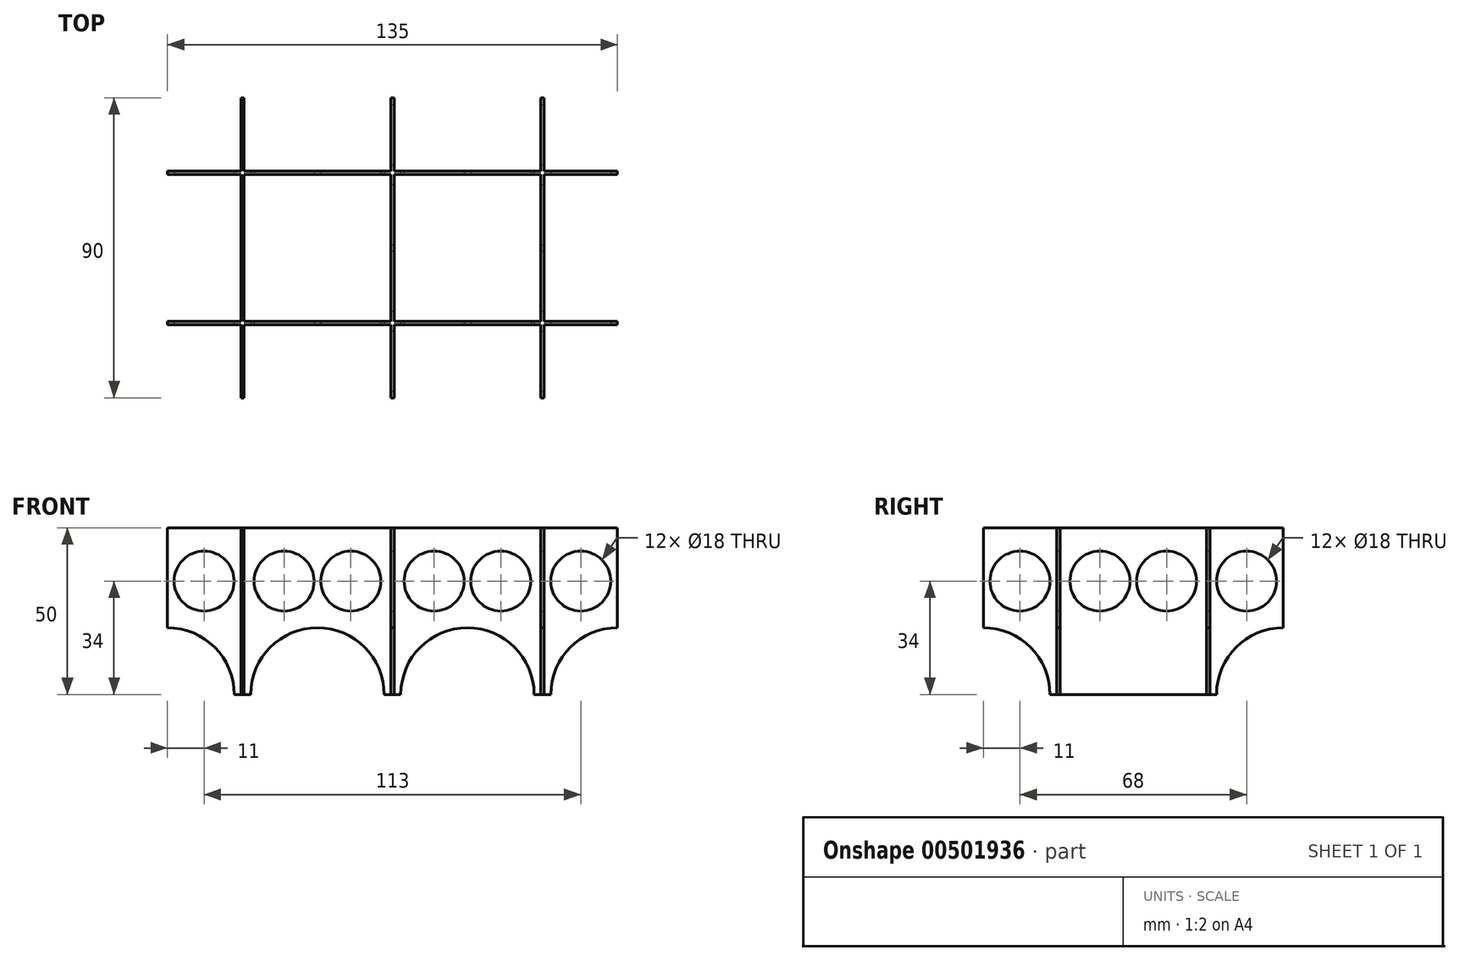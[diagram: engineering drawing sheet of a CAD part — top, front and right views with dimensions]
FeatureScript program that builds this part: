
annotation { "Feature Type Name" : "Feature", "Feature Type Description" : "" }
export const myFeature = defineFeature(function(context is Context, id is Id, definition is map)
    precondition{}
    {
        {
            var Q0;
            Q0=qCreatedBy(makeId("Top.planeOp"),FACE);
            var sketch = newSketch(context, id + "F0", { "sketchPlane" : qUnion([Q0])});
            skPoint(sketch, "E0", {"position": v(0, -22.5) * mm});
            skPoint(sketch, "E1", {"position": v(0, 22.5) * mm});
            skPoint(sketch, "E2", {"position": v(-45, 0) * mm});
            skPoint(sketch, "E3", {"position": v(45, 0) * mm});
            skLineSegment(sketch, "E4.bottom", {"start": v(67.5, 22) * mm, "end": v(-67.5, 22) * mm});
            skLineSegment(sketch, "E4.top", {"start": v(67.5, 23) * mm, "end": v(-67.5, 23) * mm});
            skLineSegment(sketch, "E4.left", {"start": v(67.5, 22) * mm, "end": v(67.5, 23) * mm});
            skLineSegment(sketch, "E4.right", {"start": v(-67.5, 22) * mm, "end": v(-67.5, 23) * mm});
            skLineSegment(sketch, "E5.bottom", {"start": v(67.5, -23) * mm, "end": v(-67.5, -23) * mm});
            skLineSegment(sketch, "E5.top", {"start": v(67.5, -22) * mm, "end": v(-67.5, -22) * mm});
            skLineSegment(sketch, "E5.left", {"start": v(67.5, -23) * mm, "end": v(67.5, -22) * mm});
            skLineSegment(sketch, "E5.right", {"start": v(-67.5, -23) * mm, "end": v(-67.5, -22) * mm});
            skLineSegment(sketch, "E6.bottom", {"start": v(-44.5, -45) * mm, "end": v(-45.5, -45) * mm});
            skLineSegment(sketch, "E6.top", {"start": v(-44.5, 45) * mm, "end": v(-45.5, 45) * mm});
            skLineSegment(sketch, "E6.left", {"start": v(-44.5, -45) * mm, "end": v(-44.5, 45) * mm});
            skLineSegment(sketch, "E6.right", {"start": v(-45.5, -45) * mm, "end": v(-45.5, 45) * mm});
            skLineSegment(sketch, "E7.bottom", {"start": v(45.5, -45) * mm, "end": v(44.5, -45) * mm});
            skLineSegment(sketch, "E7.top", {"start": v(45.5, 45) * mm, "end": v(44.5, 45) * mm});
            skLineSegment(sketch, "E7.left", {"start": v(45.5, -45) * mm, "end": v(45.5, 45) * mm});
            skLineSegment(sketch, "E7.right", {"start": v(44.5, -45) * mm, "end": v(44.5, 45) * mm});
            skLineSegment(sketch, "E8.bottom", {"start": v(0.5, -45) * mm, "end": v(-0.5, -45) * mm});
            skLineSegment(sketch, "E8.top", {"start": v(0.5, 45) * mm, "end": v(-0.5, 45) * mm});
            skLineSegment(sketch, "E8.left", {"start": v(0.5, -45) * mm, "end": v(0.5, 45) * mm});
            skLineSegment(sketch, "E8.right", {"start": v(-0.5, -45) * mm, "end": v(-0.5, 45) * mm});
            skPoint(sketch, "E8.middle", {"position": v(0, 0) * mm});
            skSolve(sketch);
        }
        {
            var Q0;
            {var subQ5=sQuery(id+"F0.wireOp",EDGE,"E6.top");Q0=makeQuery(id+"F0.imprint","IMPRINT",FACE,{"disambiguationData":[TD([[makeQuery(id+"F0.imprint","IMPRINT",EDGE,{"derivedFrom":subQ5}),1.0]])]});}
            var Q1;
            {var subQ0=sQuery(id+"F0.wireOp",EDGE,"E4.right");Q1=makeQuery(id+"F0.imprint","IMPRINT",FACE,{"disambiguationData":[TD([[makeQuery(id+"F0.imprint","IMPRINT",EDGE,{"derivedFrom":subQ0}),-1.0]])]});}
            var Q2;
            {var subQ0=sQuery(id+"F0.wireOp",EDGE,"E8.right");var subQ1=sQuery(id+"F0.wireOp",EDGE,"E4.bottom");var subQ2=makeQuery(id+"F0.imprint","INTERSECT",VERTEX,{"derivedFrom":[subQ1,subQ0]});Q2=makeQuery(id+"F0.imprint","IMPRINT",FACE,{"disambiguationData":[TD([[makeQuery(id+"F0.imprint","IMPRINT",EDGE,{"disambiguationData":[TD([[subQ2,-1.0]])],"derivedFrom":subQ1}),-1.0]])]});}
            var Q3;
            {var subQ0=sQuery(id+"F0.wireOp",EDGE,"E6.right");var subQ1=sQuery(id+"F0.wireOp",EDGE,"E4.bottom");var subQ2=makeQuery(id+"F0.imprint","INTERSECT",VERTEX,{"derivedFrom":[subQ1,subQ0]});Q3=makeQuery(id+"F0.imprint","IMPRINT",FACE,{"disambiguationData":[TD([[makeQuery(id+"F0.imprint","IMPRINT",EDGE,{"disambiguationData":[TD([[subQ2,1.0]])],"derivedFrom":subQ1}),1.0]])]});}
            var Q4;
            {var subQ0=sQuery(id+"F0.wireOp",EDGE,"E6.right");var subQ1=sQuery(id+"F0.wireOp",EDGE,"E4.bottom");var subQ2=makeQuery(id+"F0.imprint","INTERSECT",VERTEX,{"derivedFrom":[subQ1,subQ0]});Q4=makeQuery(id+"F0.imprint","IMPRINT",FACE,{"disambiguationData":[TD([[makeQuery(id+"F0.imprint","IMPRINT",EDGE,{"disambiguationData":[TD([[subQ2,1.0]])],"derivedFrom":subQ1}),-1.0]])]});}
            var Q5;
            {var subQ0=sQuery(id+"F0.wireOp",EDGE,"E8.left");var subQ1=sQuery(id+"F0.wireOp",EDGE,"E4.bottom");var subQ2=makeQuery(id+"F0.imprint","INTERSECT",VERTEX,{"derivedFrom":[subQ1,subQ0]});Q5=makeQuery(id+"F0.imprint","IMPRINT",FACE,{"disambiguationData":[TD([[makeQuery(id+"F0.imprint","IMPRINT",EDGE,{"disambiguationData":[TD([[subQ2,-1.0]])],"derivedFrom":subQ1}),-1.0]])]});}
            var Q6;
            {var subQ5=sQuery(id+"F0.wireOp",EDGE,"E8.top");Q6=makeQuery(id+"F0.imprint","IMPRINT",FACE,{"disambiguationData":[TD([[makeQuery(id+"F0.imprint","IMPRINT",EDGE,{"derivedFrom":subQ5}),1.0]])]});}
            var Q7;
            {var subQ0=sQuery(id+"F0.wireOp",EDGE,"E7.right");var subQ1=sQuery(id+"F0.wireOp",EDGE,"E4.bottom");var subQ2=makeQuery(id+"F0.imprint","INTERSECT",VERTEX,{"derivedFrom":[subQ1,subQ0]});Q7=makeQuery(id+"F0.imprint","IMPRINT",FACE,{"disambiguationData":[TD([[makeQuery(id+"F0.imprint","IMPRINT",EDGE,{"disambiguationData":[TD([[subQ2,-1.0]])],"derivedFrom":subQ1}),-1.0]])]});}
            var Q8;
            {var subQ0=sQuery(id+"F0.wireOp",EDGE,"E8.left");var subQ1=sQuery(id+"F0.wireOp",EDGE,"E4.bottom");var subQ2=makeQuery(id+"F0.imprint","INTERSECT",VERTEX,{"derivedFrom":[subQ1,subQ0]});Q8=makeQuery(id+"F0.imprint","IMPRINT",FACE,{"disambiguationData":[TD([[makeQuery(id+"F0.imprint","IMPRINT",EDGE,{"disambiguationData":[TD([[subQ2,-1.0]])],"derivedFrom":subQ1}),1.0]])]});}
            var Q9;
            {var subQ0=sQuery(id+"F0.wireOp",EDGE,"E7.left");var subQ1=sQuery(id+"F0.wireOp",EDGE,"E4.bottom");var subQ2=makeQuery(id+"F0.imprint","INTERSECT",VERTEX,{"derivedFrom":[subQ1,subQ0]});Q9=makeQuery(id+"F0.imprint","IMPRINT",FACE,{"disambiguationData":[TD([[makeQuery(id+"F0.imprint","IMPRINT",EDGE,{"disambiguationData":[TD([[subQ2,-1.0]])],"derivedFrom":subQ1}),-1.0]])]});}
            var Q10;
            {var subQ0=sQuery(id+"F0.wireOp",EDGE,"E4.left");Q10=makeQuery(id+"F0.imprint","IMPRINT",FACE,{"disambiguationData":[TD([[makeQuery(id+"F0.imprint","IMPRINT",EDGE,{"derivedFrom":subQ0}),1.0]])]});}
            var Q11;
            {var subQ5=sQuery(id+"F0.wireOp",EDGE,"E7.top");Q11=makeQuery(id+"F0.imprint","IMPRINT",FACE,{"disambiguationData":[TD([[makeQuery(id+"F0.imprint","IMPRINT",EDGE,{"derivedFrom":subQ5}),1.0]])]});}
            var Q12;
            {var subQ0=sQuery(id+"F0.wireOp",EDGE,"E7.left");var subQ1=sQuery(id+"F0.wireOp",EDGE,"E4.bottom");var subQ2=makeQuery(id+"F0.imprint","INTERSECT",VERTEX,{"derivedFrom":[subQ1,subQ0]});Q12=makeQuery(id+"F0.imprint","IMPRINT",FACE,{"disambiguationData":[TD([[makeQuery(id+"F0.imprint","IMPRINT",EDGE,{"disambiguationData":[TD([[subQ2,-1.0]])],"derivedFrom":subQ1}),1.0]])]});}
            var Q13;
            {var subQ0=sQuery(id+"F0.wireOp",EDGE,"E5.left");Q13=makeQuery(id+"F0.imprint","IMPRINT",FACE,{"disambiguationData":[TD([[makeQuery(id+"F0.imprint","IMPRINT",EDGE,{"derivedFrom":subQ0}),1.0]])]});}
            var Q14;
            {var subQ5=sQuery(id+"F0.wireOp",EDGE,"E7.bottom");Q14=makeQuery(id+"F0.imprint","IMPRINT",FACE,{"disambiguationData":[TD([[makeQuery(id+"F0.imprint","IMPRINT",EDGE,{"derivedFrom":subQ5}),-1.0]])]});}
            var Q15;
            {var subQ0=sQuery(id+"F0.wireOp",EDGE,"E7.left");var subQ1=sQuery(id+"F0.wireOp",EDGE,"E5.bottom");var subQ2=makeQuery(id+"F0.imprint","INTERSECT",VERTEX,{"derivedFrom":[subQ1,subQ0]});Q15=makeQuery(id+"F0.imprint","IMPRINT",FACE,{"disambiguationData":[TD([[makeQuery(id+"F0.imprint","IMPRINT",EDGE,{"disambiguationData":[TD([[subQ2,-1.0]])],"derivedFrom":subQ1}),-1.0]])]});}
            var Q16;
            {var subQ0=sQuery(id+"F0.wireOp",EDGE,"E7.right");var subQ1=sQuery(id+"F0.wireOp",EDGE,"E5.bottom");var subQ2=makeQuery(id+"F0.imprint","INTERSECT",VERTEX,{"derivedFrom":[subQ1,subQ0]});Q16=makeQuery(id+"F0.imprint","IMPRINT",FACE,{"disambiguationData":[TD([[makeQuery(id+"F0.imprint","IMPRINT",EDGE,{"disambiguationData":[TD([[subQ2,-1.0]])],"derivedFrom":subQ1}),-1.0]])]});}
            var Q17;
            {var subQ0=sQuery(id+"F0.wireOp",EDGE,"E8.left");var subQ1=sQuery(id+"F0.wireOp",EDGE,"E5.bottom");var subQ2=makeQuery(id+"F0.imprint","INTERSECT",VERTEX,{"derivedFrom":[subQ1,subQ0]});Q17=makeQuery(id+"F0.imprint","IMPRINT",FACE,{"disambiguationData":[TD([[makeQuery(id+"F0.imprint","IMPRINT",EDGE,{"disambiguationData":[TD([[subQ2,-1.0]])],"derivedFrom":subQ1}),-1.0]])]});}
            var Q18;
            {var subQ5=sQuery(id+"F0.wireOp",EDGE,"E8.bottom");Q18=makeQuery(id+"F0.imprint","IMPRINT",FACE,{"disambiguationData":[TD([[makeQuery(id+"F0.imprint","IMPRINT",EDGE,{"derivedFrom":subQ5}),-1.0]])]});}
            var Q19;
            {var subQ0=sQuery(id+"F0.wireOp",EDGE,"E8.right");var subQ1=sQuery(id+"F0.wireOp",EDGE,"E5.bottom");var subQ2=makeQuery(id+"F0.imprint","INTERSECT",VERTEX,{"derivedFrom":[subQ1,subQ0]});Q19=makeQuery(id+"F0.imprint","IMPRINT",FACE,{"disambiguationData":[TD([[makeQuery(id+"F0.imprint","IMPRINT",EDGE,{"disambiguationData":[TD([[subQ2,-1.0]])],"derivedFrom":subQ1}),-1.0]])]});}
            var Q20;
            {var subQ0=sQuery(id+"F0.wireOp",EDGE,"E5.right");Q20=makeQuery(id+"F0.imprint","IMPRINT",FACE,{"disambiguationData":[TD([[makeQuery(id+"F0.imprint","IMPRINT",EDGE,{"derivedFrom":subQ0}),-1.0]])]});}
            var Q21;
            {var subQ5=sQuery(id+"F0.wireOp",EDGE,"E6.bottom");Q21=makeQuery(id+"F0.imprint","IMPRINT",FACE,{"disambiguationData":[TD([[makeQuery(id+"F0.imprint","IMPRINT",EDGE,{"derivedFrom":subQ5}),-1.0]])]});}
            var Q22;
            {var subQ0=sQuery(id+"F0.wireOp",EDGE,"E6.left");var subQ1=sQuery(id+"F0.wireOp",EDGE,"E5.bottom");var subQ2=makeQuery(id+"F0.imprint","INTERSECT",VERTEX,{"derivedFrom":[subQ1,subQ0]});Q22=makeQuery(id+"F0.imprint","IMPRINT",FACE,{"disambiguationData":[TD([[makeQuery(id+"F0.imprint","IMPRINT",EDGE,{"disambiguationData":[TD([[subQ2,-1.0]])],"derivedFrom":subQ1}),-1.0]])]});}
            extrude(context, id + "F1", {"entities" : qUnion([Q0, Q1, Q2, Q3, Q4, Q5, Q6, Q7, Q8, Q9, Q10, Q11, Q12, Q13, Q14, Q15, Q16, Q17, Q18, Q19, Q20, Q21, Q22]), "depth" : 50 * mm});
        }
        {
            var Q0;
            {var subQ0=sQuery(id+"F0.wireOp",EDGE,"E5.bottom");Q0=makeQuery(id+"F1.opExtrude","SWEPT_FACE",FACE,{"disambiguationData":[OSD([subQ0]),TDD([makeQuery(id+"F0.imprint","IMPRINT",EDGE,{"disambiguationData":[TD([[makeQuery(id+"F0.imprint","INTERSECT",VERTEX,{"derivedFrom":[subQ0,sQuery(id+"F0.wireOp",EDGE,"E8.right")]}),-1.0]])],"derivedFrom":subQ0})])]});}
            var sketch = newSketch(context, id + "F2", { "sketchPlane" : qUnion([Q0])});
            skPoint(sketch, "E9", {"position": v(-22.5, 0) * mm});
            skCircle(sketch, "E10", {"center": v(-22.5, 0) * mm, "radius": 20 * mm});
            skPoint(sketch, "E11", {"position": v(-32.5, 34) * mm});
            skPoint(sketch, "E12", {"position": v(-12.5, 34) * mm});
            skCircle(sketch, "E13", {"center": v(-32.5, 34) * mm, "radius": 9 * mm});
            skCircle(sketch, "E14", {"center": v(-12.5, 34) * mm, "radius": 9 * mm});
            skPoint(sketch, "E15", {"position": v(22.5, 0) * mm});
            skCircle(sketch, "E16", {"center": v(22.5, 0) * mm, "radius": 20 * mm});
            skPoint(sketch, "E17", {"position": v(12.5, 34) * mm});
            skPoint(sketch, "E18", {"position": v(32.5, 34) * mm});
            skCircle(sketch, "E19", {"center": v(12.5, 34) * mm, "radius": 9 * mm});
            skCircle(sketch, "E20", {"center": v(32.5, 34) * mm, "radius": 9 * mm});
            skCircle(sketch, "E21", {"center": v(-67.5, 0) * mm, "radius": 20 * mm});
            skPoint(sketch, "E22", {"position": v(-56.5, 34) * mm});
            skCircle(sketch, "E23", {"center": v(-56.5, 34) * mm, "radius": 9 * mm});
            skCircle(sketch, "E24", {"center": v(67.5, 0) * mm, "radius": 20 * mm});
            skPoint(sketch, "E25", {"position": v(56.5, 34) * mm});
            skCircle(sketch, "E26", {"center": v(56.5, 34) * mm, "radius": 9 * mm});
            skSolve(sketch);
        }
        {
            var Q0;
            Q0=makeQuery(id+"F2.imprint","IMPRINT",FACE,{"disambiguationData":[TD([[makeQuery(id+"F2.imprint","IMPRINT",EDGE,{"derivedFrom":sQuery(id+"F2.wireOp",EDGE,"E23")}),1.0]])]});
            var Q1;
            Q1=makeQuery(id+"F2.imprint","IMPRINT",FACE,{"disambiguationData":[TD([[makeQuery(id+"F2.imprint","IMPRINT",EDGE,{"derivedFrom":sQuery(id+"F2.wireOp",EDGE,"E21")}),1.0]])]});
            var Q2;
            {var subQ0=sQuery(id+"F2.wireOp",EDGE,"E10");var subQ1=sQuery(id+"F0.wireOp",EDGE,"E5.bottom");var subQ2=makeQuery(id+"F1.opExtrude","CAP_EDGE",EDGE,{"disambiguationData":[OSD([subQ1]),TDD([makeQuery(id+"F0.imprint","IMPRINT",EDGE,{"disambiguationData":[TD([[makeQuery(id+"F0.imprint","INTERSECT",VERTEX,{"derivedFrom":[subQ1,sQuery(id+"F0.wireOp",EDGE,"E8.right")]}),-1.0]])],"derivedFrom":subQ1})])],"isStart":true});var subQ3=makeQuery(id+"F2.imprint","INTERSECT",VERTEX,{"disambiguationData":[OD(0.0)],"derivedFrom":[subQ2,subQ0]});Q2=makeQuery(id+"F2.imprint","IMPRINT",FACE,{"disambiguationData":[TD([[makeQuery(id+"F2.imprint","IMPRINT",EDGE,{"disambiguationData":[TD([[subQ3,-1.0]])],"derivedFrom":subQ0}),1.0]])]});}
            var Q3;
            Q3=makeQuery(id+"F2.imprint","IMPRINT",FACE,{"disambiguationData":[TD([[makeQuery(id+"F2.imprint","IMPRINT",EDGE,{"derivedFrom":sQuery(id+"F2.wireOp",EDGE,"E13")}),1.0]])]});
            var Q4;
            Q4=makeQuery(id+"F2.imprint","IMPRINT",FACE,{"disambiguationData":[TD([[makeQuery(id+"F2.imprint","IMPRINT",EDGE,{"derivedFrom":sQuery(id+"F2.wireOp",EDGE,"E14")}),1.0]])]});
            var Q5;
            Q5=makeQuery(id+"F2.imprint","IMPRINT",FACE,{"disambiguationData":[TD([[makeQuery(id+"F2.imprint","IMPRINT",EDGE,{"derivedFrom":sQuery(id+"F2.wireOp",EDGE,"E16")}),1.0]])]});
            var Q6;
            Q6=makeQuery(id+"F2.imprint","IMPRINT",FACE,{"disambiguationData":[TD([[makeQuery(id+"F2.imprint","IMPRINT",EDGE,{"derivedFrom":sQuery(id+"F2.wireOp",EDGE,"E19")}),1.0]])]});
            var Q7;
            Q7=makeQuery(id+"F2.imprint","IMPRINT",FACE,{"disambiguationData":[TD([[makeQuery(id+"F2.imprint","IMPRINT",EDGE,{"derivedFrom":sQuery(id+"F2.wireOp",EDGE,"E20")}),1.0]])]});
            var Q8;
            Q8=makeQuery(id+"F2.imprint","IMPRINT",FACE,{"disambiguationData":[TD([[makeQuery(id+"F2.imprint","IMPRINT",EDGE,{"derivedFrom":sQuery(id+"F2.wireOp",EDGE,"E26")}),1.0]])]});
            var Q9;
            Q9=makeQuery(id+"F2.imprint","IMPRINT",FACE,{"disambiguationData":[TD([[makeQuery(id+"F2.imprint","IMPRINT",EDGE,{"derivedFrom":sQuery(id+"F2.wireOp",EDGE,"E24")}),1.0]])]});
            extrude(context, id + "F3", {"entities" : qUnion([Q0, Q1, Q2, Q3, Q4, Q5, Q6, Q7, Q8, Q9]), "operationType" : NewBodyOperationType.REMOVE, "oppositeDirection" : true, "depth" : 400 * mm});
        }
        {
            var Q0;
            {var subQ0=sQuery(id+"F0.wireOp",EDGE,"E7.left");Q0=makeQuery(id+"F1.opExtrude","SWEPT_FACE",FACE,{"disambiguationData":[OSD([subQ0]),TDD([makeQuery(id+"F0.imprint","IMPRINT",EDGE,{"disambiguationData":[TD([[makeQuery(id+"F0.imprint","INTERSECT",VERTEX,{"derivedFrom":[sQuery(id+"F0.wireOp",EDGE,"E4.bottom"),subQ0]}),1.0]])],"derivedFrom":subQ0})])]});}
            var sketch = newSketch(context, id + "F4", { "sketchPlane" : qUnion([Q0])});
            skPoint(sketch, "E27", {"position": v(0, 0) * mm});
            skCircle(sketch, "E28", {"center": v(0, 0) * mm, "radius": 20 * mm});
            skPoint(sketch, "E29", {"position": v(-10, 34) * mm});
            skPoint(sketch, "E30", {"position": v(10, 34) * mm});
            skCircle(sketch, "E31", {"center": v(-10, 34) * mm, "radius": 9 * mm});
            skCircle(sketch, "E32", {"center": v(10, 34) * mm, "radius": 9 * mm});
            skCircle(sketch, "E33", {"center": v(-45, 0) * mm, "radius": 20 * mm});
            skPoint(sketch, "E34", {"position": v(-34, 34) * mm});
            skCircle(sketch, "E35", {"center": v(-34, 34) * mm, "radius": 9 * mm});
            skCircle(sketch, "E36", {"center": v(45, 0) * mm, "radius": 20 * mm});
            skPoint(sketch, "E37", {"position": v(34, 34) * mm});
            skCircle(sketch, "E38", {"center": v(34, 34) * mm, "radius": 9 * mm});
            skSolve(sketch);
        }
        {
            var Q0;
            Q0=makeQuery(id+"F4.imprint","IMPRINT",FACE,{"disambiguationData":[TD([[makeQuery(id+"F4.imprint","IMPRINT",EDGE,{"derivedFrom":sQuery(id+"F4.wireOp",EDGE,"E35")}),1.0]])]});
            var Q1;
            Q1=makeQuery(id+"F4.imprint","IMPRINT",FACE,{"disambiguationData":[TD([[makeQuery(id+"F4.imprint","IMPRINT",EDGE,{"derivedFrom":sQuery(id+"F4.wireOp",EDGE,"E31")}),1.0]])]});
            var Q2;
            Q2=makeQuery(id+"F4.imprint","IMPRINT",FACE,{"disambiguationData":[TD([[makeQuery(id+"F4.imprint","IMPRINT",EDGE,{"derivedFrom":sQuery(id+"F4.wireOp",EDGE,"E32")}),1.0]])]});
            var Q3;
            Q3=makeQuery(id+"F4.imprint","IMPRINT",FACE,{"disambiguationData":[TD([[makeQuery(id+"F4.imprint","IMPRINT",EDGE,{"derivedFrom":sQuery(id+"F4.wireOp",EDGE,"E38")}),1.0]])]});
            var Q4;
            Q4=makeQuery(id+"F4.imprint","IMPRINT",FACE,{"disambiguationData":[TD([[makeQuery(id+"F4.imprint","IMPRINT",EDGE,{"derivedFrom":sQuery(id+"F4.wireOp",EDGE,"E36")}),1.0]])]});
            var Q5;
            {var subQ0=sQuery(id+"F4.wireOp",EDGE,"E28");var subQ1=sQuery(id+"F0.wireOp",EDGE,"E7.left");var subQ2=makeQuery(id+"F1.opExtrude","CAP_EDGE",EDGE,{"disambiguationData":[OSD([subQ1]),TDD([makeQuery(id+"F0.imprint","IMPRINT",EDGE,{"disambiguationData":[TD([[makeQuery(id+"F0.imprint","INTERSECT",VERTEX,{"derivedFrom":[sQuery(id+"F0.wireOp",EDGE,"E4.bottom"),subQ1]}),1.0]])],"derivedFrom":subQ1})])],"isStart":true});var subQ3=makeQuery(id+"F4.imprint","INTERSECT",VERTEX,{"disambiguationData":[OD(0.0)],"derivedFrom":[subQ2,subQ0]});Q5=makeQuery(id+"F4.imprint","IMPRINT",FACE,{"disambiguationData":[TD([[makeQuery(id+"F4.imprint","IMPRINT",EDGE,{"disambiguationData":[TD([[subQ3,-1.0]])],"derivedFrom":subQ0}),1.0]])]});}
            var Q6;
            Q6=makeQuery(id+"F4.imprint","IMPRINT",FACE,{"disambiguationData":[TD([[makeQuery(id+"F4.imprint","IMPRINT",EDGE,{"derivedFrom":sQuery(id+"F4.wireOp",EDGE,"E33")}),1.0]])]});
            extrude(context, id + "F5", {"entities" : qUnion([Q0, Q1, Q2, Q3, Q4, Q5, Q6]), "operationType" : NewBodyOperationType.REMOVE, "oppositeDirection" : true, "depth" : 400 * mm});
        }
    });
